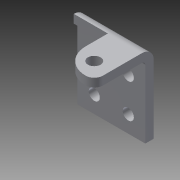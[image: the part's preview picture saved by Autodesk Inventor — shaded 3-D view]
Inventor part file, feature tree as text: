
AUTODESK INVENTOR PART (.ipt)
format: ipt  version: 2014 (Build 180170000, 170)  size: 204,800 bytes
history: native  units: in
note: dims shown in document units (in); Inventor stores cm internally (conversion verified against a paired STEP export)
features: sheet_metal_op x4, sketch x3, other x3, extrude x1, fillet x1
ambient origin geometry x8: Origin, YZ Plane, XZ Plane, XY Plane, X Axis, Y Axis, Z Axis, Center Point
bodies: Solid1 (feature_tree)
feature tree (12):
  sheet_metal_op  "Face1"
  sheet_metal_op  "Flange1"
  extrude  "Extrusion1"  Depth=1.0in
  fillet  "Fillet1"  Radius=0.164in
  sketch  "Sketch1"  dims[d0=1.0in d1=1.0in d2=0.164in]
  other  "Plate1"
  sketch  "Sketch2"  dims[d3=0.25in]
  other  "Plate2"
  sheet_metal_op  "Bend1"
  sheet_metal_op  "Corner1"
  sketch  "Sketch3"  dims[d4=0.25in d5=0.7874in d7=0.5in d8=0.7874in d10=0.5in d13=0.125in d14=0.125in d15=0.0625in d16=0.25in d17=0.125in d18=0.875in d19=90.0deg d20=0.05in d21=0.5in d22=0.125in d23=0.125in d24=0.187in d25=0.25in d26=0.25in d27=0.375in d28=0.125in d29=0.5in d30=1.0in d31=0.0in d32=0.125in]
  other  "Definition1"
